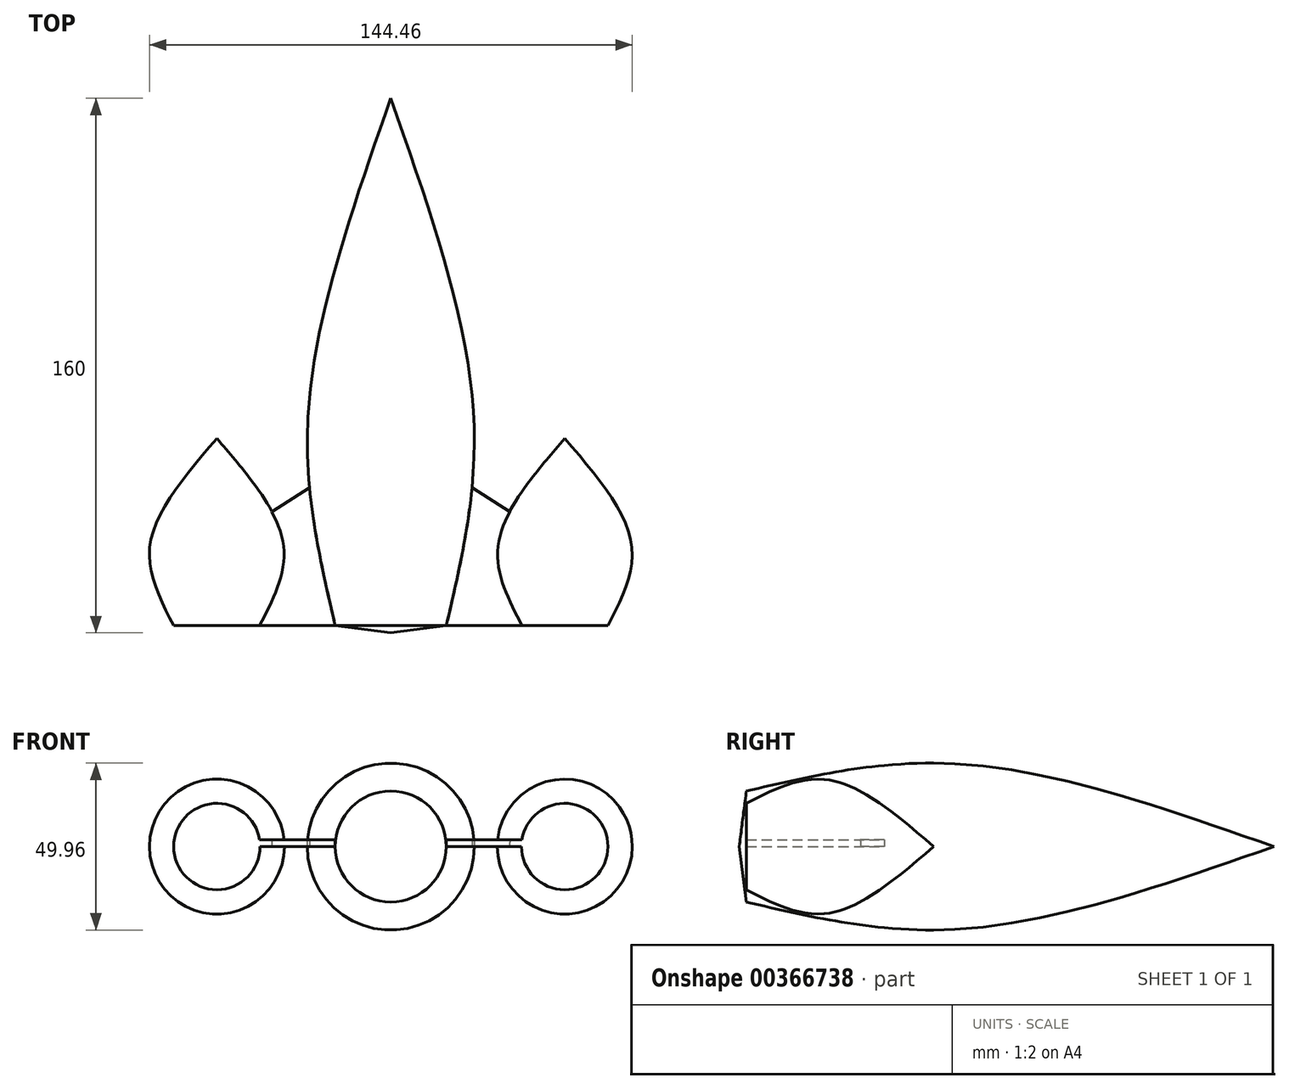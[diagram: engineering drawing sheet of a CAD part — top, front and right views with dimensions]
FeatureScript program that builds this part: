
annotation { "Feature Type Name" : "Feature", "Feature Type Description" : "" }
export const myFeature = defineFeature(function(context is Context, id is Id, definition is map)
    precondition{}
    {
        {
            var Q0;
            Q0=qCreatedBy(makeId("Top.planeOp"),FACE);
            var sketch = newSketch(context, id + "F0", { "sketchPlane" : qUnion([Q0])});
            skLineSegment(sketch, "E0", {"start": v(0, -2.16) * mm, "end": v(0, 157.84) * mm});
            skFitSpline(sketch, "E1", {"points": [v(16.61, 0) * mm, v(24.68, 64.45) * mm, v(0, 157.84) * mm], "startDerivative": vector(32.07, 136.97) * mm, "endDerivative": vector(-62.19, 177.38) * mm});
            skLineSegment(sketch, "E2", {"start": v(52.04, 0) * mm, "end": v(52.04, 56) * mm});
            skLineSegment(sketch, "E3", {"start": v(52.04, 0) * mm, "end": v(64.97, 0) * mm});
            skFitSpline(sketch, "E4", {"points": [v(64.97, 0) * mm, v(72.02, 24.26) * mm, v(52.04, 56) * mm], "startDerivative": vector(27.38, 52.92) * mm, "endDerivative": vector(-50.68, 58.89) * mm});
            skLineSegment(sketch, "E5", {"start": v(16.61, 0) * mm, "end": v(52.04, 0) * mm});
            skLineSegment(sketch, "E6", {"start": v(24.3, 41.27) * mm, "end": v(52.04, 23.67) * mm});
            skLineSegment(sketch, "E7", {"start": v(0, -2.16) * mm, "end": v(16.61, 0) * mm});
            skSolve(sketch);
        }
        {
            var Q0;
            {var subQ0=sQuery(id+"F0.wireOp",EDGE,"E3");Q0=makeQuery(id+"F0.imprint","IMPRINT",FACE,{"disambiguationData":[TD([[makeQuery(id+"F0.imprint","IMPRINT",EDGE,{"derivedFrom":subQ0}),1.0]])]});}
            var Q1;
            Q1=sQuery(id+"F0.wireOp",EDGE,"E2");
            revolve(context, id + "F1", {"entities" : qUnion([Q0]), "axis" : qUnion([Q1]), "revolveType" : RevolveType.FULL});
        }
        {
            var Q0;
            {var subQ0=sQuery(id+"F0.wireOp",EDGE,"E0");Q0=makeQuery(id+"F0.imprint","IMPRINT",FACE,{"disambiguationData":[TD([[makeQuery(id+"F0.imprint","IMPRINT",EDGE,{"derivedFrom":subQ0}),-1.0]])]});}
            var Q1;
            Q1=sQuery(id+"F0.wireOp",EDGE,"E0");
            revolve(context, id + "F2", {"entities" : qUnion([Q0]), "axis" : qUnion([Q1]), "revolveType" : RevolveType.FULL});
        }
        {
            var Q0;
            Q0=makeQuery(id+"F1.opRevolve","SWEPT_BODY",BODY,{"disambiguationData":[OSD([sQuery(id+"F0.wireOp",EDGE,"E2"),sQuery(id+"F0.wireOp",EDGE,"E3"),sQuery(id+"F0.wireOp",EDGE,"E4")])]});
            var Q1;
            Q1=qCreatedBy(makeId("Right.planeOp"),FACE);
            mirror(context, id + "F3", {"entities" : qUnion([Q0]), "mirrorPlane" : qUnion([Q1])});
        }
        {
            var Q0;
            {var subQ0=sQuery(id+"F0.wireOp",EDGE,"E5");Q0=makeQuery(id+"F0.imprint","IMPRINT",FACE,{"disambiguationData":[TD([[makeQuery(id+"F0.imprint","IMPRINT",EDGE,{"derivedFrom":subQ0}),1.0]])]});}
            extrude(context, id + "F4", {"entities" : qUnion([Q0]), "operationType" : NewBodyOperationType.ADD, "depth" : 2 * mm});
        }
        {
            var Q0;
            Q0=makeQuery(id+"F1.opRevolve","SWEPT_BODY",BODY,{"disambiguationData":[OSD([sQuery(id+"F0.wireOp",EDGE,"E2"),sQuery(id+"F0.wireOp",EDGE,"E3"),sQuery(id+"F0.wireOp",EDGE,"E4")])]});
            var Q1;
            Q1=qCreatedBy(makeId("Right.planeOp"),FACE);
            mirror(context, id + "F5", {"operationType" : NewBodyOperationType.ADD, "entities" : qUnion([Q0]), "mirrorPlane" : qUnion([Q1])});
        }
    });
